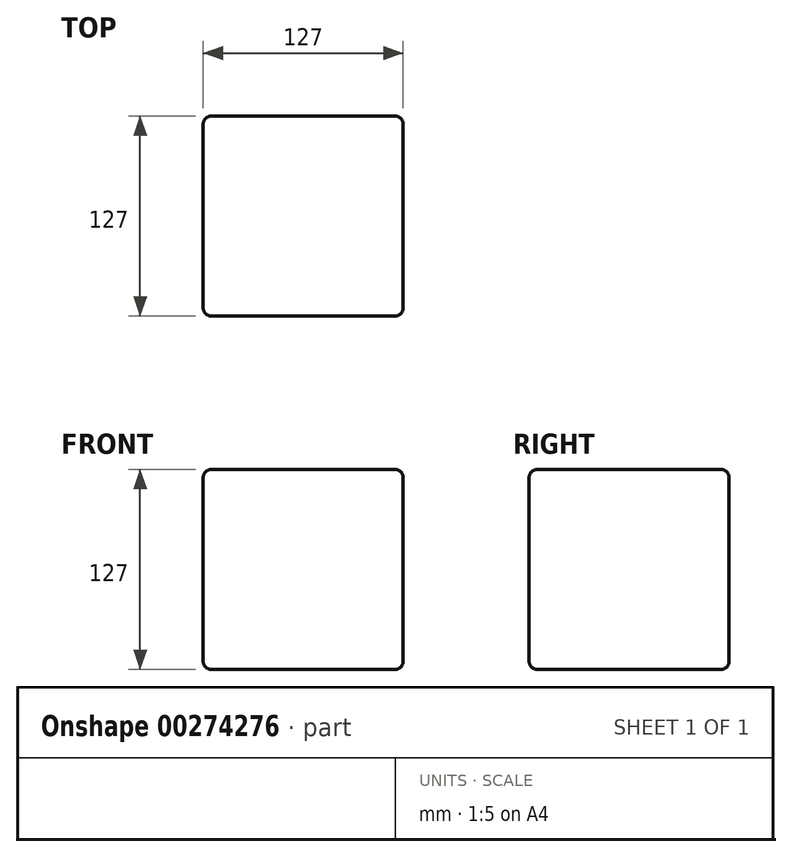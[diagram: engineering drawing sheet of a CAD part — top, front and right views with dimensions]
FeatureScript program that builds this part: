
annotation { "Feature Type Name" : "Feature", "Feature Type Description" : "" }
export const myFeature = defineFeature(function(context is Context, id is Id, definition is map)
    precondition{}
    {
        {
            var Q0;
            Q0=qCreatedBy(makeId("Top.planeOp"),FACE);
            var sketch = newSketch(context, id + "F0", { "sketchPlane" : qUnion([Q0])});
            skLineSegment(sketch, "E0.bottom", {"start": v(-79.01, -63.5) * mm, "end": v(47.99, -63.5) * mm});
            skLineSegment(sketch, "E0.top", {"start": v(-79.01, 63.5) * mm, "end": v(47.99, 63.5) * mm});
            skLineSegment(sketch, "E0.left", {"start": v(-79.01, -63.5) * mm, "end": v(-79.01, 63.5) * mm});
            skLineSegment(sketch, "E0.right", {"start": v(47.99, -63.5) * mm, "end": v(47.99, 63.5) * mm});
            skSolve(sketch);
        }
        {
            var Q0;
            Q0=makeQuery(id+"F0.imprint","IMPRINT",FACE,{"disambiguationData":[TD([[makeQuery(id+"F0.imprint","IMPRINT",EDGE,{"derivedFrom":sQuery(id+"F0.wireOp",EDGE,"E0.bottom")}),1.0]])]});
            extrude(context, id + "F1", {"entities" : qUnion([Q0]), "depth" : 127 * mm});
        }
        {
            var Q0;
            Q0=makeQuery(id+"F1.opExtrude","SWEPT_FACE",FACE,{"disambiguationData":[OSD([sQuery(id+"F0.wireOp",EDGE,"E0.bottom")])]});
            var Q1;
            Q1=makeQuery(id+"F1.opExtrude","CAP_EDGE",EDGE,{"disambiguationData":[OSD([sQuery(id+"F0.wireOp",EDGE,"E0.right")])],"isStart":true});
            var Q2;
            Q2=makeQuery(id+"F1.opExtrude","CAP_EDGE",EDGE,{"disambiguationData":[OSD([sQuery(id+"F0.wireOp",EDGE,"E0.left")])],"isStart":true});
            var Q3;
            Q3=makeQuery(id+"F1.opExtrude","CAP_EDGE",EDGE,{"disambiguationData":[OSD([sQuery(id+"F0.wireOp",EDGE,"E0.top")])],"isStart":true});
            var Q4;
            Q4=makeQuery(id+"F1.opExtrude","SWEPT_EDGE",EDGE,{"disambiguationData":[OSD([sQuery(id+"F0.wireOp",EDGE,"E0.top"),sQuery(id+"F0.wireOp",EDGE,"E0.right")])]});
            var Q5;
            Q5=makeQuery(id+"F1.opExtrude","CAP_EDGE",EDGE,{"disambiguationData":[OSD([sQuery(id+"F0.wireOp",EDGE,"E0.right")])],"isStart":false});
            var Q6;
            Q6=makeQuery(id+"F1.opExtrude","SWEPT_EDGE",EDGE,{"disambiguationData":[OSD([sQuery(id+"F0.wireOp",EDGE,"E0.top"),sQuery(id+"F0.wireOp",EDGE,"E0.left")])]});
            var Q7;
            Q7=makeQuery(id+"F1.opExtrude","CAP_EDGE",EDGE,{"disambiguationData":[OSD([sQuery(id+"F0.wireOp",EDGE,"E0.left")])],"isStart":false});
            var Q8;
            Q8=makeQuery(id+"F1.opExtrude","CAP_EDGE",EDGE,{"disambiguationData":[OSD([sQuery(id+"F0.wireOp",EDGE,"E0.top")])],"isStart":false});
            fillet(context, id + "F2", {"entities" : qUnion([Q0, Q1, Q2, Q3, Q4, Q5, Q6, Q7, Q8]), "radius" : 5.08 * mm, "tangentPropagation" : true, "allowEdgeOverflow" : false});
        }
    });
